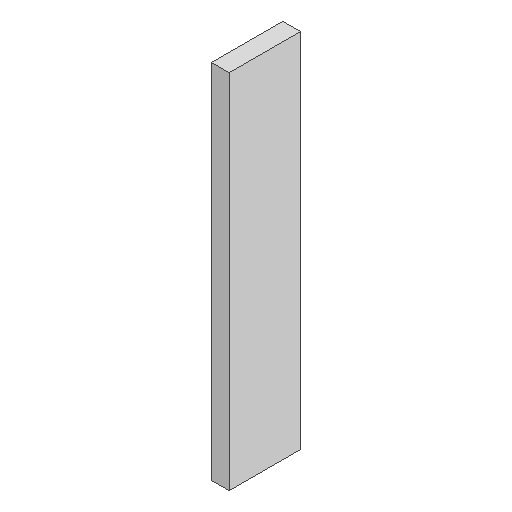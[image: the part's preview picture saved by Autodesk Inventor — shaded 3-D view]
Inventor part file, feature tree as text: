
AUTODESK INVENTOR PART (.ipt)
format: ipt  version: 2024 (Build 280153000, 153)  size: 78,848 bytes
history: native  units: mm
features: other x3, sketch x1
ambient origin geometry x8: Origin, YZ Plane, XZ Plane, XY Plane, X Axis, Y Axis, Z Axis, Center Point
bodies: Solid1 (feature_tree)
feature tree (4):
  other  "boxsectiontestcross.ipt"
  other  "Solid1::boxsectiontestcross.ipt"
  other  "TaggingFeature1"
  sketch  "Sketch1"  dims[d0=10.0mm]
